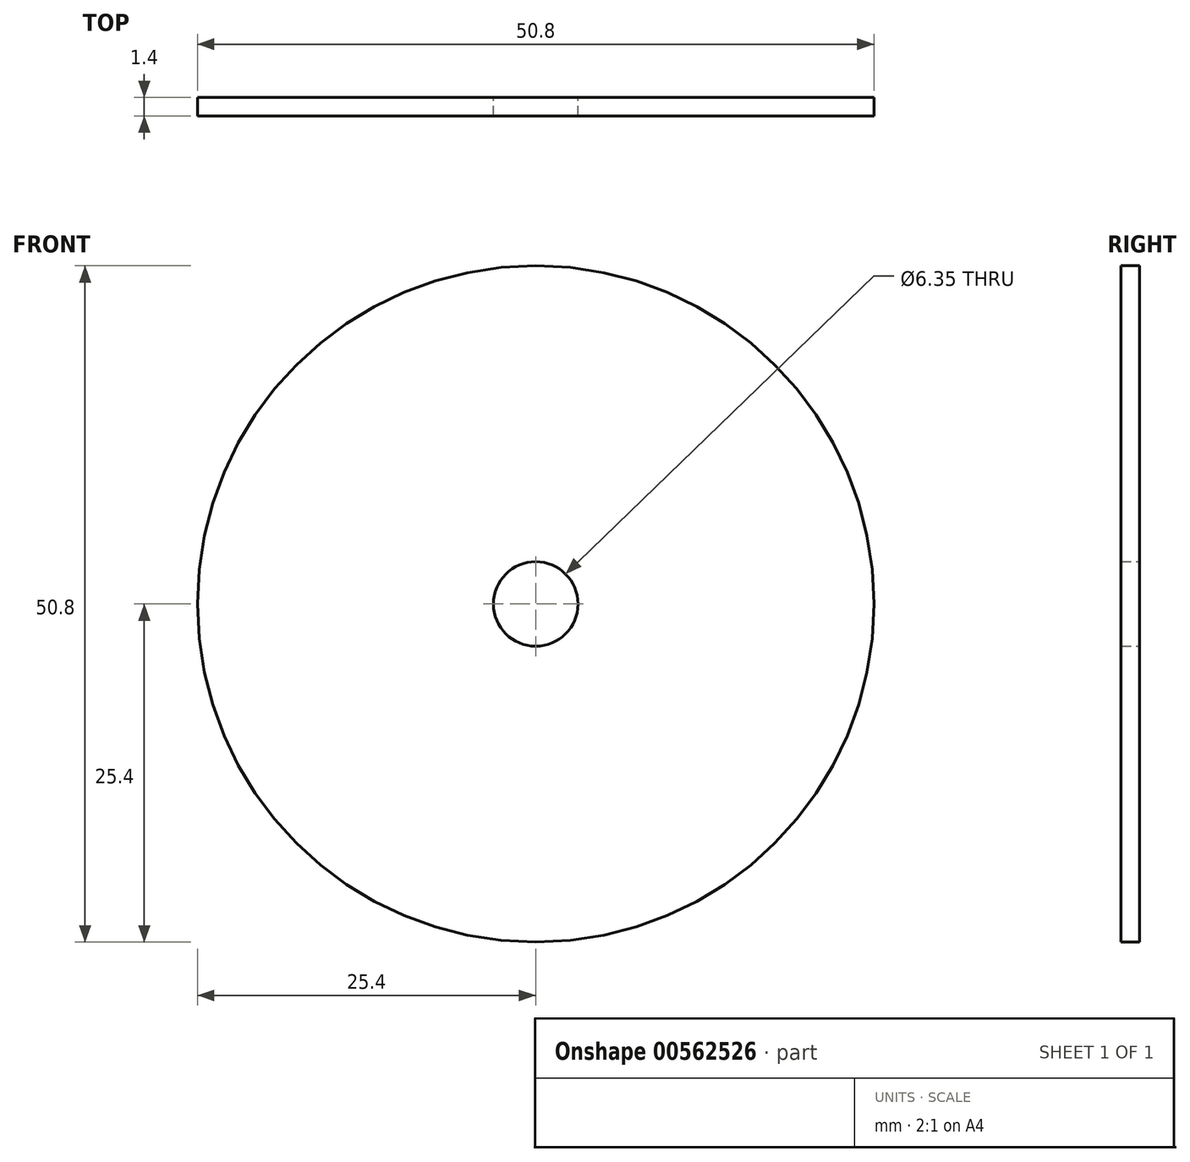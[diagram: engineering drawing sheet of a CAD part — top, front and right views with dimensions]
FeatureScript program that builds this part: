
annotation { "Feature Type Name" : "Feature", "Feature Type Description" : "" }
export const myFeature = defineFeature(function(context is Context, id is Id, definition is map)
    precondition{}
    {
        {
            var Q0;
            Q0=qCreatedBy(makeId("Front.planeOp"),FACE);
            var sketch = newSketch(context, id + "F0", { "sketchPlane" : qUnion([Q0])});
            skCircle(sketch, "E0", {"center": v(0, 0) * mm, "radius": 25.4 * mm});
            skCircle(sketch, "E1", {"center": v(0, 0) * mm, "radius": 3.18 * mm});
            skSolve(sketch);
        }
        {
            var Q0;
            Q0 = qSketchRegion(id + "F0", true);
            extrude(context, id + "F1", {"entities" : qUnion([Q0]), "depth" : 1.4 * mm, "offsetDistance" : 25.4 * mm});
        }
    });
